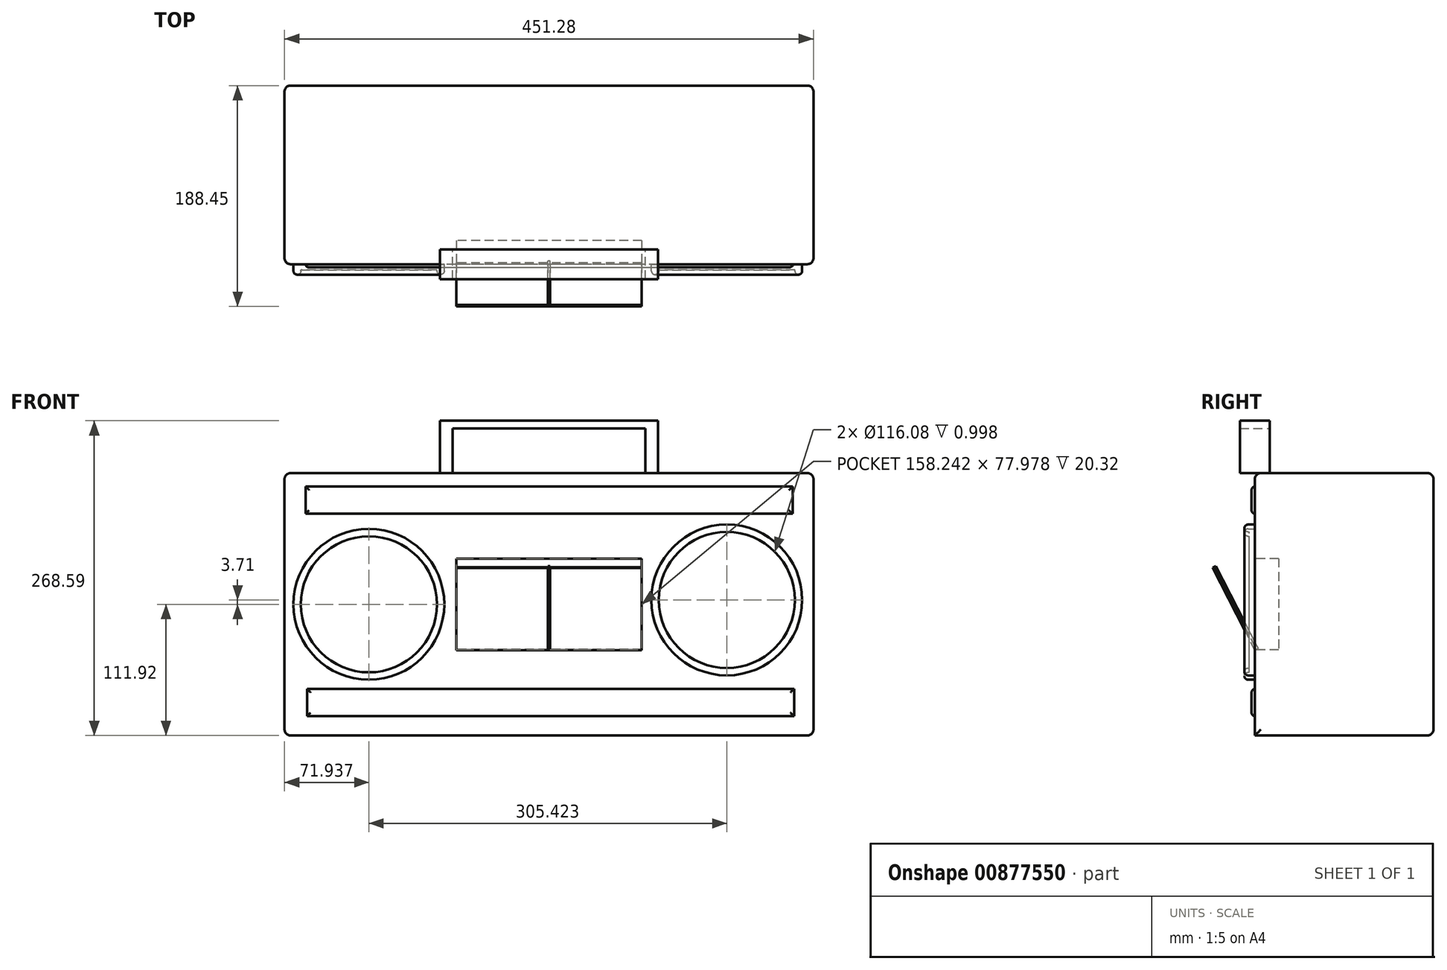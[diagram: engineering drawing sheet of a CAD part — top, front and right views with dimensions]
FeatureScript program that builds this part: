
annotation { "Feature Type Name" : "Feature", "Feature Type Description" : "" }
export const myFeature = defineFeature(function(context is Context, id is Id, definition is map)
    precondition{}
    {
        {
            var Q0;
            Q0=qCreatedBy(makeId("Front.planeOp"),FACE);
            var sketch = newSketch(context, id + "F0", { "sketchPlane" : qUnion([Q0])});
            skLineSegment(sketch, "E0.bottom", {"start": v(79.12, 38.99) * mm, "end": v(-79.12, 38.99) * mm});
            skLineSegment(sketch, "E0.top", {"start": v(79.12, -38.99) * mm, "end": v(-79.12, -38.99) * mm});
            skLineSegment(sketch, "E0.left", {"start": v(79.12, 38.99) * mm, "end": v(79.12, -38.99) * mm});
            skLineSegment(sketch, "E0.right", {"start": v(-79.12, 38.99) * mm, "end": v(-79.12, -38.99) * mm});
            skPoint(sketch, "E0.middle", {"position": v(0, 0) * mm});
            skSolve(sketch);
        }
        {
            var Q0;
            Q0=qCreatedBy(makeId("Front.planeOp"),FACE);
            var sketch = newSketch(context, id + "F1", { "sketchPlane" : qUnion([Q0])});
            skLineSegment(sketch, "E1.bottom", {"start": v(225.64, 111.92) * mm, "end": v(-225.64, 111.92) * mm});
            skLineSegment(sketch, "E1.top", {"start": v(225.64, -111.92) * mm, "end": v(-225.64, -111.92) * mm});
            skLineSegment(sketch, "E1.left", {"start": v(225.64, 111.92) * mm, "end": v(225.64, -111.92) * mm});
            skLineSegment(sketch, "E1.right", {"start": v(-225.64, 111.92) * mm, "end": v(-225.64, -111.92) * mm});
            skPoint(sketch, "E1.middle", {"position": v(0, 0) * mm});
            skSolve(sketch);
        }
        {
            var Q0;
            Q0=makeQuery(id+"F1.imprint","IMPRINT",FACE,{"disambiguationData":[TD([[makeQuery(id+"F1.imprint","IMPRINT",EDGE,{"derivedFrom":sQuery(id+"F1.wireOp",EDGE,"E1.bottom")}),1.0]])]});
            extrude(context, id + "F2", {"entities" : qUnion([Q0]), "oppositeDirection" : true, "depth" : 152.4 * mm});
        }
        {
            var Q0;
            Q0=makeQuery(id+"F0.imprint","IMPRINT",FACE,{"disambiguationData":[TD([[makeQuery(id+"F0.imprint","IMPRINT",EDGE,{"derivedFrom":sQuery(id+"F0.wireOp",EDGE,"E0.bottom")}),1.0]])]});
            extrude(context, id + "F3", {"entities" : qUnion([Q0]), "operationType" : NewBodyOperationType.REMOVE, "oppositeDirection" : true, "depth" : 20.32 * mm});
        }
        {
            var Q0;
            Q0=qCreatedBy(makeId("Front.planeOp"),FACE);
            var sketch = newSketch(context, id + "F4", { "sketchPlane" : qUnion([Q0])});
            skCircle(sketch, "E2", {"center": v(-153.7, 0) * mm, "radius": 64.33 * mm});
            skCircle(sketch, "E3", {"center": v(151.72, 3.7) * mm, "radius": 64.33 * mm});
            skCircle(sketch, "E4", {"center": v(-153.7, 0) * mm, "radius": 58.04 * mm});
            skCircle(sketch, "E5", {"center": v(151.72, 3.7) * mm, "radius": 58.04 * mm});
            skSolve(sketch);
        }
        {
            var Q0;
            Q0=makeQuery(id+"F4.imprint","IMPRINT",FACE,{"disambiguationData":[TD([[makeQuery(id+"F4.imprint","IMPRINT",EDGE,{"derivedFrom":sQuery(id+"F4.wireOp",EDGE,"E2")}),1.0]])]});
            var Q1;
            Q1=makeQuery(id+"F4.imprint","IMPRINT",FACE,{"disambiguationData":[TD([[makeQuery(id+"F4.imprint","IMPRINT",EDGE,{"derivedFrom":sQuery(id+"F4.wireOp",EDGE,"E3")}),1.0]])]});
            extrude(context, id + "F5", {"entities" : qUnion([Q0, Q1]), "operationType" : NewBodyOperationType.ADD, "depth" : 8.9 * mm});
        }
        {
            var Q0;
            Q0=makeQuery(id+"F4.imprint","IMPRINT",FACE,{"disambiguationData":[TD([[makeQuery(id+"F4.imprint","IMPRINT",EDGE,{"derivedFrom":sQuery(id+"F4.wireOp",EDGE,"E5")}),1.0]])]});
            var Q1;
            Q1=makeQuery(id+"F4.imprint","IMPRINT",FACE,{"disambiguationData":[TD([[makeQuery(id+"F4.imprint","IMPRINT",EDGE,{"derivedFrom":sQuery(id+"F4.wireOp",EDGE,"E4")}),1.0]])]});
            extrude(context, id + "F6", {"entities" : qUnion([Q0, Q1]), "operationType" : NewBodyOperationType.ADD, "depth" : 4.83 * mm});
        }
        {
            var Q0;
            Q0=qCreatedBy(makeId("Front.planeOp"),FACE);
            var sketch = newSketch(context, id + "F7", { "sketchPlane" : qUnion([Q0])});
            skLineSegment(sketch, "E6.bottom", {"start": v(207.8, 100.54) * mm, "end": v(-207.8, 100.54) * mm});
            skLineSegment(sketch, "E6.top", {"start": v(207.8, 77.23) * mm, "end": v(-207.8, 77.23) * mm});
            skLineSegment(sketch, "E6.left", {"start": v(207.8, 100.54) * mm, "end": v(207.8, 77.23) * mm});
            skLineSegment(sketch, "E6.right", {"start": v(-207.8, 100.54) * mm, "end": v(-207.8, 77.23) * mm});
            skPoint(sketch, "E6.middle", {"position": v(0, 88.89) * mm});
            skLineSegment(sketch, "E7.bottom", {"start": v(209.06, -72.15) * mm, "end": v(-206.54, -72.15) * mm});
            skLineSegment(sketch, "E7.top", {"start": v(209.06, -95.47) * mm, "end": v(-206.54, -95.47) * mm});
            skLineSegment(sketch, "E7.left", {"start": v(209.06, -72.15) * mm, "end": v(209.06, -95.47) * mm});
            skLineSegment(sketch, "E7.right", {"start": v(-206.54, -72.15) * mm, "end": v(-206.54, -95.47) * mm});
            skPoint(sketch, "E7.middle", {"position": v(1.26, -83.8) * mm});
            skSolve(sketch);
        }
        {
            var Q0;
            Q0=makeQuery(id+"F7.imprint","IMPRINT",FACE,{"disambiguationData":[TD([[makeQuery(id+"F7.imprint","IMPRINT",EDGE,{"derivedFrom":sQuery(id+"F7.wireOp",EDGE,"E6.bottom")}),1.0]])]});
            var Q1;
            Q1=makeQuery(id+"F7.imprint","IMPRINT",FACE,{"disambiguationData":[TD([[makeQuery(id+"F7.imprint","IMPRINT",EDGE,{"derivedFrom":sQuery(id+"F7.wireOp",EDGE,"E7.bottom")}),1.0]])]});
            extrude(context, id + "F8", {"entities" : qUnion([Q0, Q1]), "operationType" : NewBodyOperationType.ADD, "depth" : 2.8 * mm});
        }
        {
            var Q0;
            Q0=qCreatedBy(makeId("Right.planeOp"),FACE);
            var sketch = newSketch(context, id + "F9", { "sketchPlane" : qUnion([Q0])});
            skLineSegment(sketch, "E8", {"start": v(0, -39.04) * mm, "end": v(-36.05, 31.26) * mm});
            skLineSegment(sketch, "E9", {"start": v(-36.05, 31.26) * mm, "end": v(-33.34, 32.65) * mm});
            skLineSegment(sketch, "E10", {"start": v(0, -39.04) * mm, "end": v(2.72, -37.65) * mm});
            skLineSegment(sketch, "E11", {"start": v(-33.34, 32.65) * mm, "end": v(2.72, -37.65) * mm});
            skSolve(sketch);
        }
        {
            var Q0;
            Q0=makeQuery(id+"F9.imprint","IMPRINT",FACE,{"disambiguationData":[TD([[makeQuery(id+"F9.imprint","IMPRINT",EDGE,{"derivedFrom":sQuery(id+"F9.wireOp",EDGE,"E8")}),-1.0]])]});
            extrude(context, id + "F10", {"entities" : qUnion([Q0]), "endBound" : BoundingType.SYMMETRIC, "depth" : 1.78 * mm});
        }
        {
            var Q0;
            Q0=qCreatedBy(makeId("Right.planeOp"),FACE);
            var sketch = newSketch(context, id + "F11", { "sketchPlane" : qUnion([Q0])});
            skLineSegment(sketch, "E12", {"start": v(0, -39.04) * mm, "end": v(-35.9, 31.02) * mm});
            skLineSegment(sketch, "E13", {"start": v(-35.9, 31.02) * mm, "end": v(-34.7, 31.64) * mm});
            skLineSegment(sketch, "E14", {"start": v(-34.7, 31.64) * mm, "end": v(1.23, -38.47) * mm});
            skLineSegment(sketch, "E15", {"start": v(1.23, -38.47) * mm, "end": v(0, -39.04) * mm});
            skSolve(sketch);
        }
        {
            var Q0;
            Q0=qSketchRegion(id+"F11",true);
            extrude(context, id + "F12", {"entities" : qUnion([Q0]), "endBound" : BoundingType.SYMMETRIC, "depth" : 158 * mm});
        }
        {
            var Q0;
            Q0=qCreatedBy(makeId("Front.planeOp"),FACE);
            var sketch = newSketch(context, id + "F13", { "sketchPlane" : qUnion([Q0])});
            skLineSegment(sketch, "E16", {"start": v(-82.27, 112.02) * mm, "end": v(-82.27, 150.12) * mm});
            skLineSegment(sketch, "E17", {"start": v(-82.27, 150.12) * mm, "end": v(0, 150.12) * mm});
            skLineSegment(sketch, "E18.MirrorCS", {"start": v(82.27, 150.12) * mm, "end": v(0, 150.12) * mm});
            skLineSegment(sketch, "E19.MirrorCS", {"start": v(82.27, 112.02) * mm, "end": v(82.27, 150.12) * mm});
            skLineSegment(sketch, "E20", {"start": v(-93.02, 112.02) * mm, "end": v(-93.02, 150.12) * mm});
            skLineSegment(sketch, "E21", {"start": v(-93.02, 150.12) * mm, "end": v(-93.02, 156.67) * mm});
            skLineSegment(sketch, "E22", {"start": v(-93.02, 156.67) * mm, "end": v(0, 156.67) * mm});
            skLineSegment(sketch, "E23.MirrorCS", {"start": v(93.02, 156.67) * mm, "end": v(0, 156.67) * mm});
            skLineSegment(sketch, "E24.MirrorCS", {"start": v(93.02, 150.12) * mm, "end": v(93.02, 156.67) * mm});
            skLineSegment(sketch, "E25.MirrorCS", {"start": v(93.02, 112.02) * mm, "end": v(93.02, 150.12) * mm});
            skLineSegment(sketch, "E26", {"start": v(-93.02, 112.02) * mm, "end": v(-82.27, 112.02) * mm});
            skLineSegment(sketch, "E27", {"start": v(82.27, 112.02) * mm, "end": v(93.02, 112.02) * mm});
            skSolve(sketch);
        }
        {
            var Q0;
            Q0=makeQuery(id+"F13.imprint","IMPRINT",FACE,{"disambiguationData":[TD([[makeQuery(id+"F13.imprint","IMPRINT",EDGE,{"derivedFrom":sQuery(id+"F13.wireOp",EDGE,"E16")}),1.0]])]});
            extrude(context, id + "F14", {"entities" : qUnion([Q0]), "endBound" : BoundingType.SYMMETRIC, "depth" : 25.4 * mm});
        }
        {
            var Q0;
            Q0=makeQuery(id+"F5.opExtrude","CAP_EDGE",EDGE,{"disambiguationData":[OSD([sQuery(id+"F4.wireOp",EDGE,"E4")])],"isStart":false});
            var Q1;
            Q1=makeQuery(id+"F5.opExtrude","CAP_EDGE",EDGE,{"disambiguationData":[OSD([sQuery(id+"F4.wireOp",EDGE,"E2")])],"isStart":false});
            var Q2;
            Q2=makeQuery(id+"F5.opExtrude","CAP_EDGE",EDGE,{"disambiguationData":[OSD([sQuery(id+"F4.wireOp",EDGE,"E3")])],"isStart":false});
            var Q3;
            Q3=makeQuery(id+"F5.opExtrude","CAP_EDGE",EDGE,{"disambiguationData":[OSD([sQuery(id+"F4.wireOp",EDGE,"E5")])],"isStart":false});
            fillet(context, id + "F15", {"entities" : qUnion([Q0, Q1, Q2, Q3]), "radius" : 3.07 * mm, "tangentPropagation" : true, "allowEdgeOverflow" : false});
        }
        {
            var Q0;
            Q0=makeQuery(id+"F8.opExtrude","CAP_EDGE",EDGE,{"disambiguationData":[OSD([sQuery(id+"F7.wireOp",EDGE,"E6.bottom")])],"isStart":false});
            var Q1;
            Q1=makeQuery(id+"F8.opExtrude","CAP_EDGE",EDGE,{"disambiguationData":[OSD([sQuery(id+"F7.wireOp",EDGE,"E6.top")])],"isStart":false});
            var Q2;
            Q2=makeQuery(id+"F8.opExtrude","CAP_EDGE",EDGE,{"disambiguationData":[OSD([sQuery(id+"F7.wireOp",EDGE,"E6.right")])],"isStart":false});
            var Q3;
            Q3=makeQuery(id+"F8.opExtrude","CAP_EDGE",EDGE,{"disambiguationData":[OSD([sQuery(id+"F7.wireOp",EDGE,"E6.left")])],"isStart":false});
            var Q4;
            Q4=makeQuery(id+"F8.opExtrude","CAP_EDGE",EDGE,{"disambiguationData":[OSD([sQuery(id+"F7.wireOp",EDGE,"E7.bottom")])],"isStart":false});
            var Q5;
            Q5=makeQuery(id+"F8.opExtrude","CAP_EDGE",EDGE,{"disambiguationData":[OSD([sQuery(id+"F7.wireOp",EDGE,"E7.left")])],"isStart":false});
            var Q6;
            Q6=makeQuery(id+"F8.opExtrude","CAP_EDGE",EDGE,{"disambiguationData":[OSD([sQuery(id+"F7.wireOp",EDGE,"E7.top")])],"isStart":false});
            var Q7;
            Q7=makeQuery(id+"F8.opExtrude","CAP_EDGE",EDGE,{"disambiguationData":[OSD([sQuery(id+"F7.wireOp",EDGE,"E7.right")])],"isStart":false});
            fillet(context, id + "F16", {"entities" : qUnion([Q0, Q1, Q2, Q3, Q4, Q5, Q6, Q7]), "radius" : 3.07 * mm, "tangentPropagation" : true, "allowEdgeOverflow" : false});
        }
        {
            var Q0;
            Q0=makeQuery(id+"F2.opExtrude","CAP_EDGE",EDGE,{"disambiguationData":[OSD([sQuery(id+"F1.wireOp",EDGE,"E1.right")])],"isStart":true});
            var Q1;
            Q1=makeQuery(id+"F2.opExtrude","CAP_EDGE",EDGE,{"disambiguationData":[OSD([sQuery(id+"F1.wireOp",EDGE,"E1.right")])],"isStart":false});
            var Q2;
            Q2=makeQuery(id+"F2.opExtrude","CAP_EDGE",EDGE,{"disambiguationData":[OSD([sQuery(id+"F1.wireOp",EDGE,"E1.left")])],"isStart":true});
            var Q3;
            Q3=makeQuery(id+"F2.opExtrude","CAP_EDGE",EDGE,{"disambiguationData":[OSD([sQuery(id+"F1.wireOp",EDGE,"E1.left")])],"isStart":false});
            var Q4;
            Q4=makeQuery(id+"F2.opExtrude","SWEPT_EDGE",EDGE,{"disambiguationData":[OSD([sQuery(id+"F1.wireOp",EDGE,"E1.top"),sQuery(id+"F1.wireOp",EDGE,"E1.left")])]});
            var Q5;
            Q5=makeQuery(id+"F2.opExtrude","SWEPT_EDGE",EDGE,{"disambiguationData":[OSD([sQuery(id+"F1.wireOp",EDGE,"E1.bottom"),sQuery(id+"F1.wireOp",EDGE,"E1.left")])]});
            var Q6;
            Q6=makeQuery(id+"F2.opExtrude","CAP_EDGE",EDGE,{"disambiguationData":[OSD([sQuery(id+"F1.wireOp",EDGE,"E1.bottom")])],"isStart":true});
            var Q7;
            Q7=makeQuery(id+"F2.opExtrude","CAP_EDGE",EDGE,{"disambiguationData":[OSD([sQuery(id+"F1.wireOp",EDGE,"E1.bottom")])],"isStart":false});
            var Q8;
            Q8=makeQuery(id+"F2.opExtrude","CAP_EDGE",EDGE,{"disambiguationData":[OSD([sQuery(id+"F1.wireOp",EDGE,"E1.top")])],"isStart":false});
            var Q9;
            Q9=makeQuery(id+"F2.opExtrude","SWEPT_EDGE",EDGE,{"disambiguationData":[OSD([sQuery(id+"F1.wireOp",EDGE,"E1.top"),sQuery(id+"F1.wireOp",EDGE,"E1.right")])]});
            var Q10;
            Q10=makeQuery(id+"F2.opExtrude","SWEPT_EDGE",EDGE,{"disambiguationData":[OSD([sQuery(id+"F1.wireOp",EDGE,"E1.bottom"),sQuery(id+"F1.wireOp",EDGE,"E1.right")])]});
            fillet(context, id + "F17", {"entities" : qUnion([Q0, Q1, Q2, Q3, Q4, Q5, Q6, Q7, Q8, Q9, Q10]), "radius" : 5.08 * mm, "tangentPropagation" : true, "allowEdgeOverflow" : false});
        }
    });
